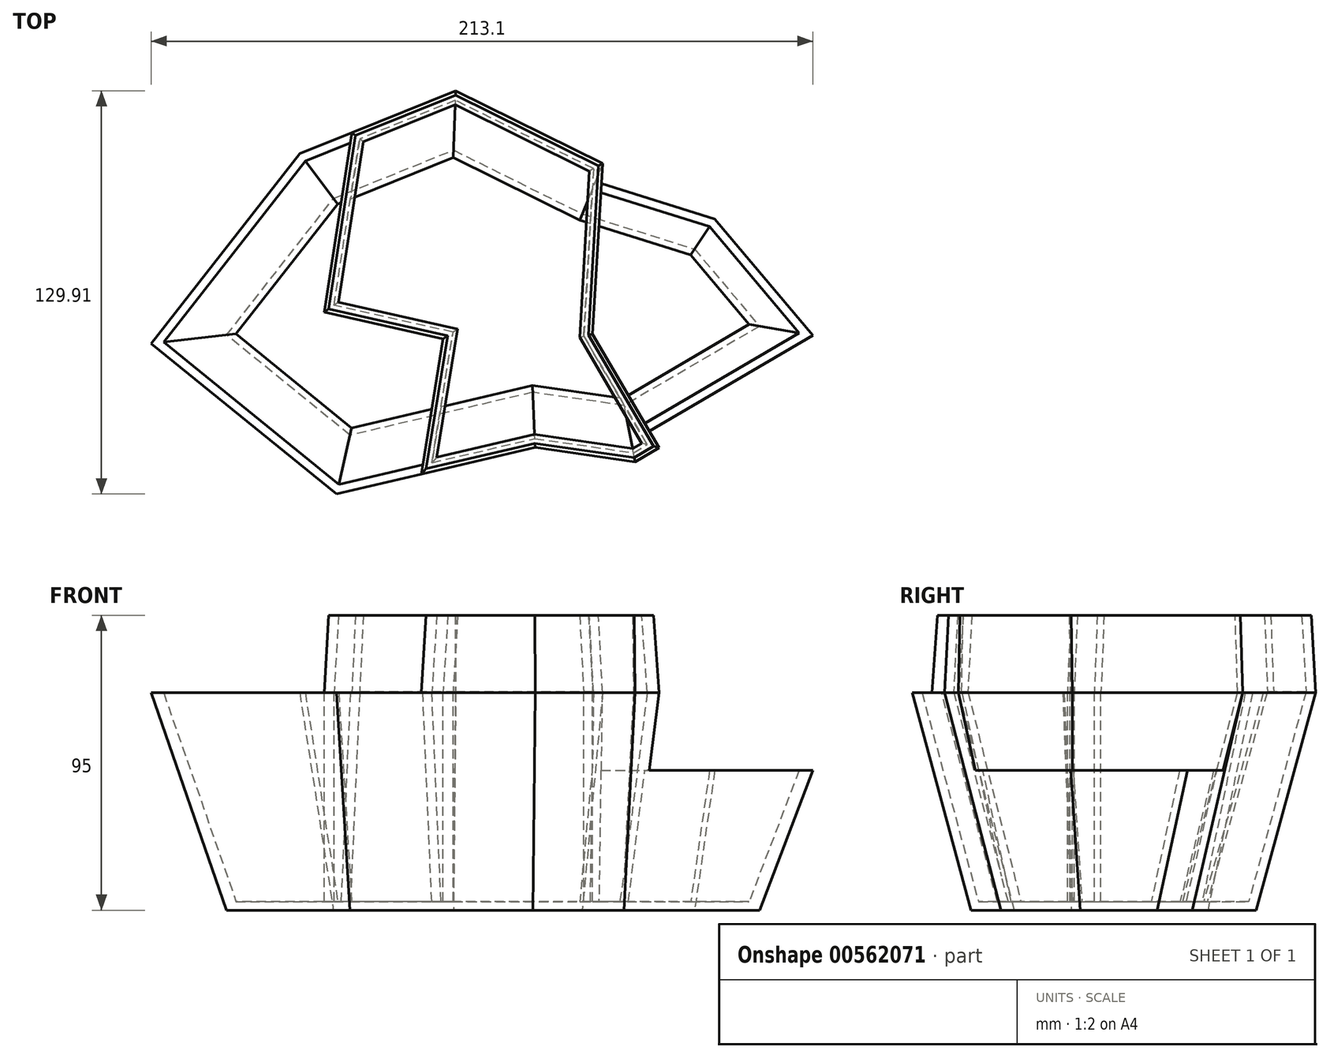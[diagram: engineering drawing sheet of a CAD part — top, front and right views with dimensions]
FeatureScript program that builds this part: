
annotation { "Feature Type Name" : "Feature", "Feature Type Description" : "" }
export const myFeature = defineFeature(function(context is Context, id is Id, definition is map)
    precondition{}
    {
        {
            var Q0;
            Q0=qCreatedBy(makeId("Top.planeOp"),FACE);
            var sketch = newSketch(context, id + "F0", { "sketchPlane" : qUnion([Q0])});
            skLineSegment(sketch, "E0", {"start": v(-78.01, -16.67) * mm, "end": v(-38.3, -48.94) * mm});
            skLineSegment(sketch, "E1", {"start": v(-38.3, -48.94) * mm, "end": v(20.57, -35.1) * mm});
            skLineSegment(sketch, "E2", {"start": v(20.57, -35.1) * mm, "end": v(50, -39.36) * mm});
            skLineSegment(sketch, "E3", {"start": v(50, -39.36) * mm, "end": v(93.62, -13.83) * mm});
            skLineSegment(sketch, "E4", {"start": v(93.62, -13.83) * mm, "end": v(72.7, 11) * mm});
            skLineSegment(sketch, "E5", {"start": v(72.7, 11) * mm, "end": v(36.53, 22.34) * mm});
            skLineSegment(sketch, "E6", {"start": v(36.53, 22.34) * mm, "end": v(-4.96, 42.9) * mm});
            skLineSegment(sketch, "E7", {"start": v(-4.96, 42.9) * mm, "end": v(-43.62, 27.3) * mm});
            skLineSegment(sketch, "E8", {"start": v(-43.62, 27.3) * mm, "end": v(-78.01, -16.67) * mm});
            skSolve(sketch);
        }
        {
            var Q0;
            Q0=makeQuery(id+"F0.imprint","IMPRINT",FACE,{"disambiguationData":[TD([[makeQuery(id+"F0.imprint","IMPRINT",EDGE,{"derivedFrom":sQuery(id+"F0.wireOp",EDGE,"E0")}),1.0]])]});
            extrude(context, id + "F1", {"entities" : qUnion([Q0]), "depth" : 70 * mm, "offsetDistance" : 25 * mm, "hasDraft" : true, "draftAngle" : 14 * degree});
        }
        {
            var Q0;
            Q0=makeQuery(id+"F1.opExtrude","CAP_FACE",FACE,{"disambiguationData":[OSD([sQuery(id+"F0.wireOp",EDGE,"E0"),sQuery(id+"F0.wireOp",EDGE,"E1"),sQuery(id+"F0.wireOp",EDGE,"E2"),sQuery(id+"F0.wireOp",EDGE,"E3"),sQuery(id+"F0.wireOp",EDGE,"E4"),sQuery(id+"F0.wireOp",EDGE,"E5"),sQuery(id+"F0.wireOp",EDGE,"E6"),sQuery(id+"F0.wireOp",EDGE,"E7"),sQuery(id+"F0.wireOp",EDGE,"E8")])],"isStart":false});
            var sketch = newSketch(context, id + "F2", { "sketchPlane" : qUnion([Q0])});
            skLineSegment(sketch, "E9.0.0", {"start": v(-4.23, 62.02) * mm, "end": v(-37.7, 48.51) * mm});
            skLineSegment(sketch, "E9.0.3", {"start": v(-15.37, -61.48) * mm, "end": v(21.34, -52.85) * mm});
            skLineSegment(sketch, "E9.0.4", {"start": v(21.34, -52.85) * mm, "end": v(53.55, -57.5) * mm});
            skLineSegment(sketch, "E9.0.5", {"start": v(53.55, -57.5) * mm, "end": v(61.28, -52.98) * mm});
            skLineSegment(sketch, "E9.0.8", {"start": v(43.05, 38.58) * mm, "end": v(-4.23, 62.02) * mm});
            skLineSegment(sketch, "E10", {"start": v(-37.7, 48.51) * mm, "end": v(-46.62, -9.28) * mm});
            skLineSegment(sketch, "E11", {"start": v(-46.62, -9.28) * mm, "end": v(-8.3, -17.87) * mm});
            skLineSegment(sketch, "E12", {"start": v(-8.3, -17.87) * mm, "end": v(-15.37, -61.48) * mm});
            skLineSegment(sketch, "E13", {"start": v(43.05, 38.58) * mm, "end": v(39.84, -16.36) * mm});
            skLineSegment(sketch, "E14", {"start": v(39.84, -16.36) * mm, "end": v(61.28, -52.98) * mm});
            skPoint(sketch, "E9.0.2.end.orphan", {"position": v(-42.65, -67.89) * mm});
            skPoint(sketch, "E9.0.2.start.orphan", {"position": v(-102.32, -19.4) * mm});
            skPoint(sketch, "E15.orphan", {"position": v(-54.48, 41.74) * mm});
            skPoint(sketch, "E9.0.6.end.orphan", {"position": v(82.77, 26.13) * mm});
            skPoint(sketch, "E16.orphan", {"position": v(120.32, -18.42) * mm});
            skSolve(sketch);
        }
        {
            var Q0;
            Q0 = qSketchRegion(id + "F2", true);
            extrude(context, id + "F3", {"entities" : qUnion([Q0]), "operationType" : NewBodyOperationType.ADD, "depth" : 25 * mm, "offsetDistance" : 25 * mm, "hasDraft" : true, "draftAngle" : 3 * degree, "draftPullDirection" : true});
        }
        {
            var Q0;
            {var subQ0=sQuery(id+"F0.wireOp",EDGE,"E6");var subQ1=sQuery(id+"F0.wireOp",EDGE,"E5");var subQ2=sQuery(id+"F0.wireOp",EDGE,"E4");var subQ3=sQuery(id+"F0.wireOp",EDGE,"E3");Q0=makeQuery(id+"F3.boolean.opBoolean","SPLIT",FACE,{"disambiguationData":[TD([makeQuery(id+"F1.opExtrude","SWEPT_FACE",FACE,{"disambiguationData":[OSD([subQ3])]})])],"derivedFrom":makeQuery(id+"F1.opExtrude","CAP_FACE",FACE,{"disambiguationData":[OSD([sQuery(id+"F0.wireOp",EDGE,"E0"),sQuery(id+"F0.wireOp",EDGE,"E1"),sQuery(id+"F0.wireOp",EDGE,"E2"),subQ3,subQ2,subQ1,subQ0,sQuery(id+"F0.wireOp",EDGE,"E7"),sQuery(id+"F0.wireOp",EDGE,"E8")])],"isStart":false})});}
            var sketch = newSketch(context, id + "F4", { "sketchPlane" : qUnion([Q0])});
            skLineSegment(sketch, "E17.0.0", {"start": v(43.05, 38.58) * mm, "end": v(39.84, -16.36) * mm});
            skLineSegment(sketch, "E17.0.1", {"start": v(39.84, -16.36) * mm, "end": v(61.28, -52.98) * mm});
            skLineSegment(sketch, "E17.0.2", {"start": v(61.28, -52.98) * mm, "end": v(120.32, -18.42) * mm});
            skLineSegment(sketch, "E17.0.3", {"start": v(120.32, -18.42) * mm, "end": v(82.77, 26.13) * mm});
            skLineSegment(sketch, "E17.0.4", {"start": v(82.77, 26.13) * mm, "end": v(43.05, 38.58) * mm});
            skSolve(sketch);
        }
        {
            var Q0;
            Q0 = qSketchRegion(id + "F4", true);
            extrude(context, id + "F5", {"entities" : qUnion([Q0]), "operationType" : NewBodyOperationType.REMOVE, "oppositeDirection" : true, "depth" : 25 * mm, "offsetDistance" : 25 * mm});
        }
        {
            var Q0;
            {var subQ0=sQuery(id+"F0.wireOp",EDGE,"E7");var subQ1=sQuery(id+"F0.wireOp",EDGE,"E1");var subQ2=sQuery(id+"F0.wireOp",EDGE,"E8");var subQ3=sQuery(id+"F0.wireOp",EDGE,"E0");Q0=makeQuery(id+"F3.boolean.opBoolean","SPLIT",FACE,{"disambiguationData":[TD([makeQuery(id+"F1.opExtrude","SWEPT_FACE",FACE,{"disambiguationData":[OSD([subQ3])]})])],"derivedFrom":makeQuery(id+"F1.opExtrude","CAP_FACE",FACE,{"disambiguationData":[OSD([subQ3,subQ1,sQuery(id+"F0.wireOp",EDGE,"E2"),sQuery(id+"F0.wireOp",EDGE,"E3"),sQuery(id+"F0.wireOp",EDGE,"E4"),sQuery(id+"F0.wireOp",EDGE,"E5"),sQuery(id+"F0.wireOp",EDGE,"E6"),subQ0,subQ2])],"isStart":false})});}
            var Q1;
            Q1=makeQuery(id+"F3.opExtrude","CAP_FACE",FACE,{"disambiguationData":[OSD([sQuery(id+"F2.wireOp",EDGE,"E9.0.0"),sQuery(id+"F2.wireOp",EDGE,"E9.0.3"),sQuery(id+"F2.wireOp",EDGE,"E9.0.4"),sQuery(id+"F2.wireOp",EDGE,"E9.0.5"),sQuery(id+"F2.wireOp",EDGE,"E9.0.8"),sQuery(id+"F2.wireOp",EDGE,"E10"),sQuery(id+"F2.wireOp",EDGE,"E11"),sQuery(id+"F2.wireOp",EDGE,"E12"),sQuery(id+"F2.wireOp",EDGE,"E13"),sQuery(id+"F2.wireOp",EDGE,"E14")])],"isStart":false});
            var Q2;
            Q2=makeQuery(id+"F5.boolean.opBoolean","COPY",FACE,{"derivedFrom":makeQuery(id+"F5.opExtrude","CAP_FACE",FACE,{"disambiguationData":[OSD([sQuery(id+"F4.wireOp",EDGE,"E17.0.0"),sQuery(id+"F4.wireOp",EDGE,"E17.0.1"),sQuery(id+"F4.wireOp",EDGE,"E17.0.2"),sQuery(id+"F4.wireOp",EDGE,"E17.0.3"),sQuery(id+"F4.wireOp",EDGE,"E17.0.4")])],"isStart":false})});
            shell(context, id + "F6", {"entities" : qUnion([Q0, Q1, Q2]), "thickness" : 2.8 * mm});
        }
        {
            var Q0;
            Q0=makeQuery(id+"F6.opShell","OFFSET_FACE",FACE,{"disambiguationData":[OSD([sQuery(id+"F4.wireOp",EDGE,"E17.0.0"),sQuery(id+"F4.wireOp",EDGE,"E17.0.1"),sQuery(id+"F4.wireOp",EDGE,"E17.0.2"),sQuery(id+"F4.wireOp",EDGE,"E17.0.3"),sQuery(id+"F4.wireOp",EDGE,"E17.0.4")])]});
            var sketch = newSketch(context, id + "F7", { "sketchPlane" : qUnion([Q0])});
            skLineSegment(sketch, "E18.0.0", {"start": v(42.5, -29.2) * mm, "end": v(39.84, 16.36) * mm});
            skLineSegment(sketch, "E18.0.1", {"start": v(39.84, 16.36) * mm, "end": v(56.67, 45.11) * mm});
            skLineSegment(sketch, "E18.0.2", {"start": v(54.26, 46.53) * mm, "end": v(56.67, 45.11) * mm});
            skLineSegment(sketch, "E18.0.3", {"start": v(54.26, 46.53) * mm, "end": v(37, 17.04) * mm});
            skLineSegment(sketch, "E18.0.4", {"start": v(37, 17.04) * mm, "end": v(39.75, -30.06) * mm});
            skLineSegment(sketch, "E18.0.5", {"start": v(42.5, -29.2) * mm, "end": v(39.75, -30.06) * mm});
            skSolve(sketch);
        }
        {
            var Q0;
            Q0 = qSketchRegion(id + "F7", true);
            extrude(context, id + "F8", {"entities" : qUnion([Q0]), "operationType" : NewBodyOperationType.ADD, "endBound" : BoundingType.UP_TO_NEXT, "depth" : 25 * mm, "offsetDistance" : 25 * mm});
        }
        {
            var Q0;
            {var subQ0=sQuery(id+"F0.wireOp",EDGE,"E7");var subQ1=sQuery(id+"F0.wireOp",EDGE,"E1");var subQ2=sQuery(id+"F0.wireOp",EDGE,"E8");var subQ3=sQuery(id+"F0.wireOp",EDGE,"E0");var subQ4=sQuery(id+"F0.wireOp",EDGE,"E6");var subQ5=sQuery(id+"F0.wireOp",EDGE,"E5");var subQ6=sQuery(id+"F0.wireOp",EDGE,"E4");var subQ7=sQuery(id+"F0.wireOp",EDGE,"E3");var subQ8=sQuery(id+"F0.wireOp",EDGE,"E2");Q0=makeQuery(id+"F6.opShell","OFFSET_FACE",FACE,{"disambiguationData":[OSD([subQ3,subQ1,subQ8,subQ7,subQ6,subQ5,subQ4,subQ0,subQ2]),TDD([makeQuery(id+"F3.boolean.opBoolean","SPLIT",FACE,{"disambiguationData":[TD([makeQuery(id+"F1.opExtrude","SWEPT_FACE",FACE,{"disambiguationData":[OSD([subQ3])]})])],"derivedFrom":makeQuery(id+"F1.opExtrude","CAP_FACE",FACE,{"disambiguationData":[OSD([subQ3,subQ1,subQ8,subQ7,subQ6,subQ5,subQ4,subQ0,subQ2])],"isStart":false})})])]});}
            var sketch = newSketch(context, id + "F9", { "sketchPlane" : qUnion([Q0])});
            skLineSegment(sketch, "E19.0.0", {"start": v(-46.62, 9.28) * mm, "end": v(-8.3, 17.87) * mm});
            skLineSegment(sketch, "E19.0.1", {"start": v(-38.22, -45.2) * mm, "end": v(-46.62, 9.28) * mm});
            skLineSegment(sketch, "E19.0.2", {"start": v(-35.2, -46.42) * mm, "end": v(-38.22, -45.2) * mm});
            skLineSegment(sketch, "E19.0.3", {"start": v(-35.2, -46.42) * mm, "end": v(-43.45, 7.12) * mm});
            skLineSegment(sketch, "E19.0.4", {"start": v(-43.45, 7.12) * mm, "end": v(-5.1, 15.7) * mm});
            skLineSegment(sketch, "E19.0.5", {"start": v(-5.1, 15.7) * mm, "end": v(-11.92, 57.7) * mm});
            skLineSegment(sketch, "E19.0.6", {"start": v(-14.87, 58.4) * mm, "end": v(-11.92, 57.7) * mm});
            skLineSegment(sketch, "E19.0.7", {"start": v(-8.3, 17.87) * mm, "end": v(-14.87, 58.4) * mm});
            skSolve(sketch);
        }
        {
            var Q0;
            Q0 = qSketchRegion(id + "F9", true);
            extrude(context, id + "F10", {"entities" : qUnion([Q0]), "operationType" : NewBodyOperationType.ADD, "endBound" : BoundingType.UP_TO_NEXT, "depth" : 25 * mm, "offsetDistance" : 25 * mm});
        }
    });
